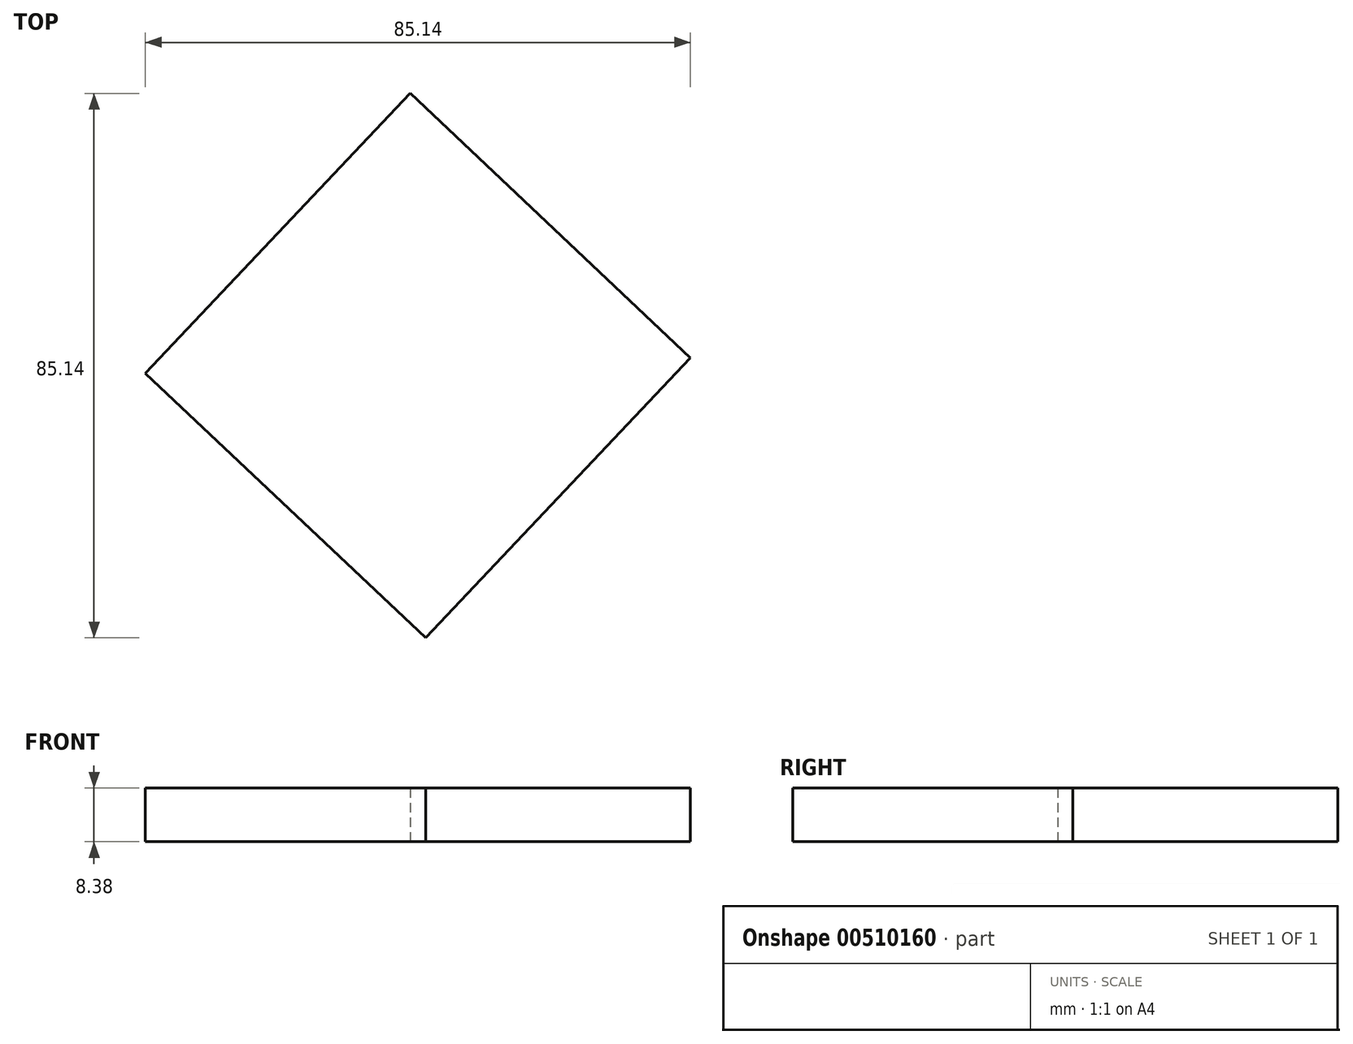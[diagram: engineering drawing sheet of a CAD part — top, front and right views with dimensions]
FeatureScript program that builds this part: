
annotation { "Feature Type Name" : "Feature", "Feature Type Description" : "" }
export const myFeature = defineFeature(function(context is Context, id is Id, definition is map)
    precondition{}
    {
        {
            var Q0;
            Q0=qCreatedBy(makeId("Top.planeOp"),FACE);
            var sketch = newSketch(context, id + "F0", { "sketchPlane" : qUnion([Q0])});
            skCircle(sketch, "E0.cCircle", {"center": v(0, 0) * mm, "radius": 30.12 * mm, "construction": true});
            skLineSegment(sketch, "E0.0", {"start": v(-1.2, 42.57) * mm, "end": v(42.57, 1.2) * mm});
            skLineSegment(sketch, "E0.1", {"start": v(42.57, 1.2) * mm, "end": v(1.2, -42.57) * mm});
            skLineSegment(sketch, "E0.2", {"start": v(1.2, -42.57) * mm, "end": v(-42.57, -1.2) * mm});
            skLineSegment(sketch, "E0.3", {"start": v(-42.57, -1.2) * mm, "end": v(-1.2, 42.57) * mm});
            skPoint(sketch, "E0.0.midPoint", {"position": v(20.69, 21.88) * mm});
            skSolve(sketch);
        }
        {
            var Q0;
            Q0=makeQuery(id+"F0.imprint","IMPRINT",FACE,{"disambiguationData":[TD([[makeQuery(id+"F0.imprint","IMPRINT",EDGE,{"derivedFrom":sQuery(id+"F0.wireOp",EDGE,"E0.0")}),-1.0]])]});
            extrude(context, id + "F1", {"entities" : qUnion([Q0]), "depth" : 8.38 * mm, "offsetDistance" : 25.4 * mm});
        }
    });
